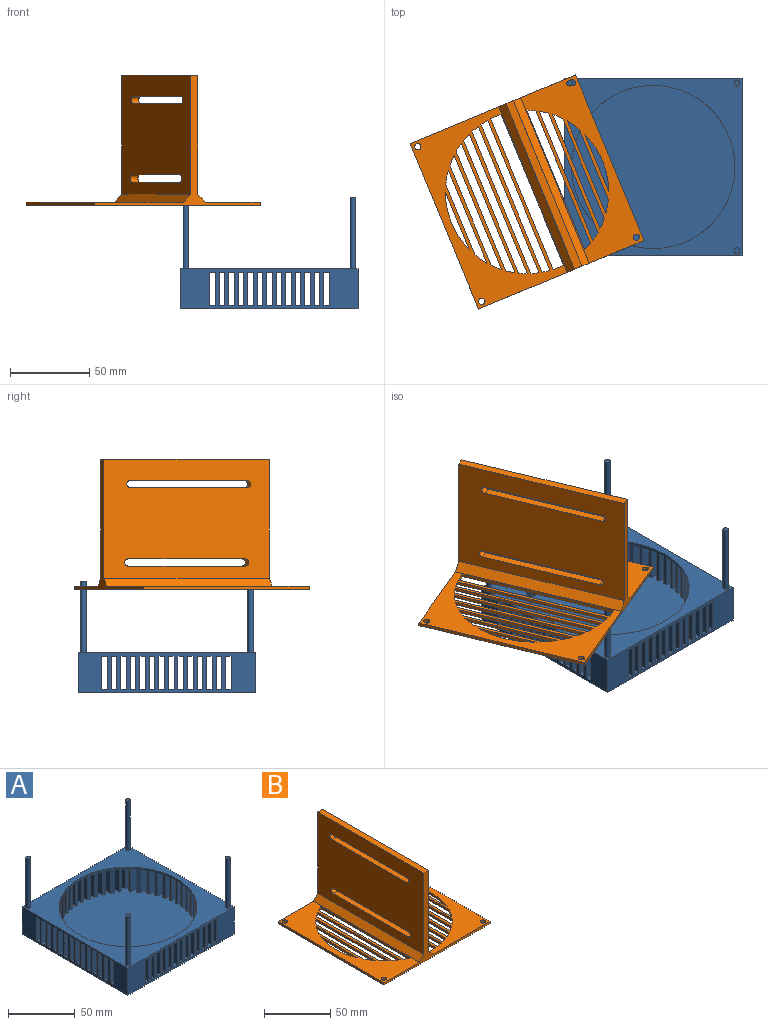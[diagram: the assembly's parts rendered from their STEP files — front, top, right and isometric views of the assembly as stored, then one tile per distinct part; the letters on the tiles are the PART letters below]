
ASSEMBLY  parts=2 mates=1
PART A: 178 faces, bbox 112x112x70 mm
  f0: plane 112x25mm, normal (0,-1,0), area 1844.5mm2, adj f9,f10,f11,f12,f22,f24,f26,f113
  f1: plane 112x25mm, normal (0,1,0), area 1844.5mm2, adj f9,f10,f11,f12,f22,f100,f102,f104
  f2: plane 21x2.5mm, normal (0,1,0), area 52.5mm2, adj f22,f24,f118,f120
  f3: plane 21x18.5mm, normal (0,-1,0), area 388.5mm2, adj f10,f22,f26,f115
  f4: plane 21x18.5mm, normal (0,1,0), area 388.5mm2, adj f10,f22,f26,f114
  f5: plane 21x2.5mm, normal (0,-1,0), area 52.5mm2, adj f22,f100,f109,f111
  f6: plane 21x2.5mm, normal (0,-1,0), area 52.5mm2, adj f22,f102,f104,f106
  f7: plane 21x18.5mm, normal (0,-1,0), area 388.5mm2, adj f10,f22,f102,f105
  f8: plane 21x18.5mm, normal (0,1,0), area 388.5mm2, adj f10,f22,f102,f103
  f9: plane 112x25mm, normal (1,0,0), area 1771mm2, adj f0,f1,f11,f12,f22,f23,f24,f25
  f10: plane 112x25mm, normal (-1,0,0), area 1771mm2, adj f0,f1,f3,f4,f7,f8,f11,f12
  f11: plane 112x112mm, normal (0,0,1), area 4173.2mm2, adj f0,f1,f9,f10,f13,f15,f17,f19
  f12: plane 112x112mm, normal (0,0,-1), area 12544mm2, adj f0,f1,f9,f10
  f13: cylinder r=1.75mm len=45mm, axis (0,0,-1), area 494.8mm2, adj f11,f14
  f14: plane 3.5x3.5mm, normal (0,0,1), area 9.6mm2, adj f13
  f15: cylinder r=1.75mm len=45mm, axis (0,0,-1), area 494.8mm2, adj f11,f16
  f16: plane 3.5x3.5mm, normal (0,0,1), area 9.6mm2, adj f15
  f17: cylinder r=1.75mm len=45mm, axis (0,0,-1), area 494.8mm2, adj f11,f18
  f18: plane 3.5x3.5mm, normal (0,0,1), area 9.6mm2, adj f17
  f19: cylinder r=1.75mm len=45mm, axis (0,0,-1), area 494.8mm2, adj f11,f20
  f20: plane 3.5x3.5mm, normal (0,0,1), area 9.6mm2, adj f19
  f21: cylinder r=51.5mm len=103mm, axis (0,0,1), area 3066.7mm2, adj f11,f22,f24,f26,f27,f28,f29,f30
  f22: plane 112x112mm, normal (0,0,1), area 10264.7mm2, adj f0,f1,f2,f3,f4,f5,f6,f7
  f23: plane 21x18mm, normal (0,1,0), area 378mm2, adj f9,f22,f24,f119
  f24: plane 27.5x21.24mm, normal (0,0,-1), area 184.2mm2, adj f0,f2,f9,f21,f23,f25,f116,f117
  f25: plane 21x18mm, normal (0,-1,0), area 378mm2, adj f9,f22,f24,f116
  f26: plane 24.19x20.7mm, normal (0,0,-1), area 133.1mm2, adj f0,f3,f4,f10,f21,f27,f113,f114
  f27: plane 21x2.19mm, normal (0,1,0), area 45.9mm2, adj f21,f22,f26,f113
  f28: plane 21x17.76mm, normal (0,1,0), area 373mm2, adj f9,f21,f22,f29
  f29: plane 17.76x3.5mm, normal (0,0,-1), area 57mm2, adj f9,f21,f28,f30
  f30: plane 21x14.88mm, normal (0,-1,0), area 312.4mm2, adj f9,f21,f22,f29
  f31: plane 17.76x3.5mm, normal (0,0,-1), area 57mm2, adj f10,f21,f32,f33
  f32: plane 21x14.88mm, normal (0,-1,0), area 312.4mm2, adj f10,f21,f22,f31
  f33: plane 21x17.76mm, normal (0,1,0), area 373mm2, adj f10,f21,f22,f31
  f34: plane 21x13.1mm, normal (0,1,0), area 275.2mm2, adj f9,f21,f22,f35
  f35: plane 13.1x3.5mm, normal (0,0,-1), area 42mm2, adj f9,f21,f34,f36
  f36: plane 21x10.98mm, normal (0,-1,0), area 230.5mm2, adj f9,f21,f22,f35
  f37: plane 13.1x3.5mm, normal (0,0,-1), area 42mm2, adj f10,f21,f38,f39
  f38: plane 21x10.98mm, normal (0,-1,0), area 230.5mm2, adj f10,f21,f22,f37
  f39: plane 21x13.1mm, normal (0,1,0), area 275.2mm2, adj f10,f21,f22,f37
  f40: plane 21x9.68mm, normal (0,1,0), area 203.2mm2, adj f9,f21,f22,f41
  f41: plane 9.68x3.5mm, normal (0,0,-1), area 31.1mm2, adj f9,f21,f40,f42
  f42: plane 21x8.13mm, normal (0,-1,0), area 170.8mm2, adj f9,f21,f22,f41
  f43: plane 9.68x3.5mm, normal (0,0,-1), area 31.1mm2, adj f10,f21,f44,f45
  f44: plane 21x8.13mm, normal (0,-1,0), area 170.8mm2, adj f10,f21,f22,f43
  f45: plane 21x9.68mm, normal (0,1,0), area 203.2mm2, adj f10,f21,f22,f43
  f46: plane 21x7.21mm, normal (0,1,0), area 151.5mm2, adj f9,f21,f22,f47
  f47: plane 7.21x3.5mm, normal (0,0,-1), area 23.3mm2, adj f9,f21,f46,f48
  f48: plane 21x6.17mm, normal (0,-1,0), area 129.5mm2, adj f9,f21,f22,f47
  f49: plane 7.21x3.5mm, normal (0,0,-1), area 23.3mm2, adj f10,f21,f50,f51
  f50: plane 21x6.17mm, normal (0,-1,0), area 129.5mm2, adj f10,f21,f22,f49
  f51: plane 21x7.21mm, normal (0,1,0), area 151.5mm2, adj f10,f21,f22,f49
  f52: plane 21x5.58mm, normal (0,1,0), area 117.2mm2, adj f9,f21,f22,f53
  f53: plane 5.58x3.5mm, normal (0,0,-1), area 18.4mm2, adj f9,f21,f52,f54
  f54: plane 21x4.98mm, normal (0,-1,0), area 104.5mm2, adj f9,f21,f22,f53
  f55: plane 5.58x3.5mm, normal (0,0,-1), area 18.4mm2, adj f10,f21,f56,f57
  f56: plane 21x4.98mm, normal (0,-1,0), area 104.5mm2, adj f10,f21,f22,f55
  f57: plane 21x5.58mm, normal (0,1,0), area 117.2mm2, adj f10,f21,f22,f55
  f58: plane 21x4.7mm, normal (0,1,0), area 98.6mm2, adj f9,f21,f22,f59
  f59: plane 4.7x3.5mm, normal (0,0,-1), area 16mm2, adj f9,f21,f58,f60
  f60: plane 21x4.51mm, normal (0,-1,0), area 94.7mm2, adj f9,f21,f22,f59
  f61: plane 4.7x3.5mm, normal (0,0,-1), area 16mm2, adj f10,f21,f62,f63
  f62: plane 21x4.51mm, normal (0,-1,0), area 94.7mm2, adj f10,f21,f22,f61
  f63: plane 21x4.7mm, normal (0,1,0), area 98.6mm2, adj f10,f21,f22,f61
  f64: plane 21x4.52mm, normal (0,1,0), area 95mm2, adj f9,f21,f22,f65
  f65: plane 4.74x3.5mm, normal (0,0,-1), area 16.1mm2, adj f9,f21,f64,f66
  f66: plane 21x4.74mm, normal (0,-1,0), area 99.6mm2, adj f9,f21,f22,f65
  f67: plane 4.74x3.5mm, normal (0,0,-1), area 16.1mm2, adj f10,f21,f68,f69
  f68: plane 21x4.74mm, normal (0,-1,0), area 99.6mm2, adj f10,f21,f22,f67
  f69: plane 21x4.52mm, normal (0,1,0), area 95mm2, adj f10,f21,f22,f67
  f70: plane 21x5.05mm, normal (0,1,0), area 106mm2, adj f9,f21,f22,f71
  f71: plane 5.69x3.5mm, normal (0,0,-1), area 18.7mm2, adj f9,f21,f70,f72
  f72: plane 21x5.69mm, normal (0,-1,0), area 119.5mm2, adj f9,f21,f22,f71
  f73: plane 5.69x3.5mm, normal (0,0,-1), area 18.7mm2, adj f10,f21,f74,f75
  f74: plane 21x5.69mm, normal (0,-1,0), area 119.5mm2, adj f10,f21,f22,f73
  f75: plane 21x5.05mm, normal (0,1,0), area 106mm2, adj f10,f21,f22,f73
  f76: plane 21x6.3mm, normal (0,1,0), area 132.3mm2, adj f9,f21,f22,f77
  f77: plane 7.39x3.5mm, normal (0,0,-1), area 23.9mm2, adj f9,f21,f76,f78
  f78: plane 21x7.39mm, normal (0,-1,0), area 155.1mm2, adj f9,f21,f22,f77
  f79: plane 7.39x3.5mm, normal (0,0,-1), area 23.9mm2, adj f10,f21,f80,f81
  f80: plane 21x7.39mm, normal (0,-1,0), area 155.1mm2, adj f10,f21,f22,f79
  f81: plane 21x6.3mm, normal (0,1,0), area 132.3mm2, adj f10,f21,f22,f79
  f82: plane 21x8.33mm, normal (0,1,0), area 175mm2, adj f9,f21,f22,f83
  f83: plane 9.92x3.5mm, normal (0,0,-1), area 31.9mm2, adj f9,f21,f82,f84
  f84: plane 21x9.92mm, normal (0,-1,0), area 208.3mm2, adj f9,f21,f22,f83
  f85: plane 9.92x3.5mm, normal (0,0,-1), area 31.9mm2, adj f10,f21,f86,f87
  f86: plane 21x9.92mm, normal (0,-1,0), area 208.3mm2, adj f10,f21,f22,f85
  f87: plane 21x8.33mm, normal (0,1,0), area 175mm2, adj f10,f21,f22,f85
  f88: plane 21x11.26mm, normal (0,1,0), area 236.4mm2, adj f9,f21,f22,f89
  f89: plane 13.44x3.5mm, normal (0,0,-1), area 43.1mm2, adj f9,f21,f88,f90
  f90: plane 21x13.44mm, normal (0,-1,0), area 282.3mm2, adj f9,f21,f22,f89
  f91: plane 13.44x3.5mm, normal (0,0,-1), area 43.1mm2, adj f10,f21,f92,f93
  f92: plane 21x13.44mm, normal (0,-1,0), area 282.3mm2, adj f10,f21,f22,f91
  f93: plane 21x11.26mm, normal (0,1,0), area 236.4mm2, adj f10,f21,f22,f91
  f94: plane 21x15.26mm, normal (0,1,0), area 320.4mm2, adj f9,f21,f22,f100
  f95: plane 21x18mm, normal (0,-1,0), area 378mm2, adj f9,f22,f100,f112
  f96: plane 18.22x3.5mm, normal (0,0,-1), area 58.4mm2, adj f10,f21,f97,f98
  f97: plane 21x18.22mm, normal (0,-1,0), area 382.6mm2, adj f10,f21,f22,f96
  f98: plane 21x15.26mm, normal (0,1,0), area 320.4mm2, adj f10,f21,f22,f96
  f99: plane 21x18mm, normal (0,1,0), area 378mm2, adj f9,f22,f100,f112
  f100: plane 27.5x24.5mm, normal (0,0,-1), area 243.9mm2, adj f1,f5,f9,f21,f94,f95,f99,f101
  f101: plane 21x18mm, normal (0,-1,0), area 378mm2, adj f9,f22,f100,f110
  f102: plane 28x20.7mm, normal (0,0,-1), area 183.2mm2, adj f1,f6,f7,f8,f10,f21,f103,f104
  f103: plane 21x2.2mm, normal (1,0,0), area 46.2mm2, adj f8,f21,f22,f102
  f104: plane 21x15mm, normal (-1,0,0), area 315mm2, adj f1,f6,f22,f102
  f105: plane 21x15mm, normal (1,0,0), area 315mm2, adj f1,f7,f22,f102
  f106: plane 21x15mm, normal (1,0,0), area 315mm2, adj f1,f6,f22,f102
  f107: plane 21x12.78mm, normal (-1,0,0), area 268.3mm2, adj f1,f21,f22,f102
  f108: plane 21x13.1mm, normal (1,0,0), area 275.2mm2, adj f1,f21,f22,f100
  f109: plane 21x15mm, normal (-1,0,0), area 315mm2, adj f1,f5,f22,f100
  f110: plane 21x15mm, normal (-1,0,0), area 315mm2, adj f1,f22,f100,f101
  f111: plane 21x15mm, normal (1,0,0), area 315mm2, adj f1,f5,f22,f100
  f112: plane 21x2.5mm, normal (-1,0,0), area 52.5mm2, adj f22,f95,f99,f100
  f113: plane 21x15.5mm, normal (-1,0,0), area 325.5mm2, adj f0,f22,f26,f27
  f114: plane 21x15.5mm, normal (1,0,0), area 325.5mm2, adj f0,f4,f22,f26
  f115: plane 21x1.7mm, normal (1,0,0), area 35.7mm2, adj f3,f21,f22,f26
  f116: plane 21x2.24mm, normal (-1,0,0), area 47mm2, adj f21,f22,f24,f25
  f117: plane 21x13.1mm, normal (1,0,0), area 275.2mm2, adj f0,f21,f22,f24
  f118: plane 21x15.5mm, normal (-1,0,0), area 325.5mm2, adj f0,f2,f22,f24
  f119: plane 21x15.5mm, normal (-1,0,0), area 325.5mm2, adj f0,f22,f23,f24
  f120: plane 21x15.5mm, normal (1,0,0), area 325.5mm2, adj f0,f2,f22,f24
  f121: plane 15.26x3.5mm, normal (0,0,-1), area 48.9mm2, adj f0,f21,f122,f123
  f122: plane 21x12.78mm, normal (-1,0,0), area 268.3mm2, adj f0,f21,f22,f121
  f123: plane 21x15.26mm, normal (1,0,0), area 320.4mm2, adj f0,f21,f22,f121
  f124: plane 21x11.26mm, normal (1,0,0), area 236.4mm2, adj f0,f21,f22,f125
  f125: plane 11.26x3.5mm, normal (0,0,-1), area 36.1mm2, adj f0,f21,f124,f126
  f126: plane 21x9.44mm, normal (-1,0,0), area 198.1mm2, adj f0,f21,f22,f125
  f127: plane 11.26x3.5mm, normal (0,0,-1), area 36.1mm2, adj f1,f21,f128,f129
  f128: plane 21x9.44mm, normal (-1,0,0), area 198.1mm2, adj f1,f21,f22,f127
  f129: plane 21x11.26mm, normal (1,0,0), area 236.4mm2, adj f1,f21,f22,f127
  f130: plane 21x8.33mm, normal (1,0,0), area 175mm2, adj f0,f21,f22,f131
  f131: plane 8.33x3.5mm, normal (0,0,-1), area 26.8mm2, adj f0,f21,f130,f132
  f132: plane 21x7.05mm, normal (-1,0,0), area 148mm2, adj f0,f21,f22,f131
  f133: plane 8.33x3.5mm, normal (0,0,-1), area 26.8mm2, adj f1,f21,f134,f135
  f134: plane 21x7.05mm, normal (-1,0,0), area 148mm2, adj f1,f21,f22,f133
  f135: plane 21x8.33mm, normal (1,0,0), area 175mm2, adj f1,f21,f22,f133
  f136: plane 21x6.3mm, normal (1,0,0), area 132.3mm2, adj f0,f21,f22,f137
  f137: plane 6.3x3.5mm, normal (0,0,-1), area 20.5mm2, adj f0,f21,f136,f138
  f138: plane 21x5.48mm, normal (-1,0,0), area 115.1mm2, adj f0,f21,f22,f137
  f139: plane 6.3x3.5mm, normal (0,0,-1), area 20.5mm2, adj f1,f21,f140,f141
  f140: plane 21x5.48mm, normal (-1,0,0), area 115.1mm2, adj f1,f21,f22,f139
  f141: plane 21x6.3mm, normal (1,0,0), area 132.3mm2, adj f1,f21,f22,f139
  f142: plane 21x5.05mm, normal (1,0,0), area 106mm2, adj f0,f21,f22,f143
  f143: plane 5.05x3.5mm, normal (0,0,-1), area 16.9mm2, adj f0,f21,f142,f144
  f144: plane 21x4.66mm, normal (-1,0,0), area 97.8mm2, adj f0,f21,f22,f143
  f145: plane 5.05x3.5mm, normal (0,0,-1), area 16.9mm2, adj f1,f21,f146,f147
  f146: plane 21x4.66mm, normal (-1,0,0), area 97.8mm2, adj f1,f21,f22,f145
  f147: plane 21x5.05mm, normal (1,0,0), area 106mm2, adj f1,f21,f22,f145
  f148: plane 21x4.52mm, normal (1,0,0), area 95mm2, adj f0,f21,f22,f149
  f149: plane 4.54x3.5mm, normal (0,0,-1), area 15.8mm2, adj f0,f21,f148,f150
  f150: plane 21x4.54mm, normal (-1,0,0), area 95.3mm2, adj f0,f21,f22,f149
  f151: plane 4.54x3.5mm, normal (0,0,-1), area 15.8mm2, adj f1,f21,f152,f153
  f152: plane 21x4.54mm, normal (-1,0,0), area 95.3mm2, adj f1,f21,f22,f151
  f153: plane 21x4.52mm, normal (1,0,0), area 95mm2, adj f1,f21,f22,f151
  f154: plane 21x4.7mm, normal (1,0,0), area 98.6mm2, adj f0,f21,f22,f155
  f155: plane 5.13x3.5mm, normal (0,0,-1), area 17.1mm2, adj f0,f21,f154,f156
  f156: plane 21x5.13mm, normal (-1,0,0), area 107.6mm2, adj f0,f21,f22,f155
  f157: plane 5.13x3.5mm, normal (0,0,-1), area 17.1mm2, adj f1,f21,f158,f159
  f158: plane 21x5.13mm, normal (-1,0,0), area 107.6mm2, adj f1,f21,f22,f157
  f159: plane 21x4.7mm, normal (1,0,0), area 98.6mm2, adj f1,f21,f22,f157
  f160: plane 21x5.58mm, normal (1,0,0), area 117.2mm2, adj f0,f21,f22,f161
  f161: plane 6.44x3.5mm, normal (0,0,-1), area 21mm2, adj f0,f21,f160,f162
  f162: plane 21x6.44mm, normal (-1,0,0), area 135.2mm2, adj f0,f21,f22,f161
  f163: plane 6.44x3.5mm, normal (0,0,-1), area 21mm2, adj f1,f21,f164,f165
  f164: plane 21x6.44mm, normal (-1,0,0), area 135.2mm2, adj f1,f21,f22,f163
  f165: plane 21x5.58mm, normal (1,0,0), area 117.2mm2, adj f1,f21,f22,f163
  f166: plane 21x7.21mm, normal (1,0,0), area 151.5mm2, adj f0,f21,f22,f167
  f167: plane 8.54x3.5mm, normal (0,0,-1), area 27.5mm2, adj f0,f21,f166,f168
  f168: plane 21x8.54mm, normal (-1,0,0), area 179.4mm2, adj f0,f21,f22,f167
  f169: plane 8.54x3.5mm, normal (0,0,-1), area 27.5mm2, adj f1,f21,f170,f171
  f170: plane 21x8.54mm, normal (-1,0,0), area 179.4mm2, adj f1,f21,f22,f169
  f171: plane 21x7.21mm, normal (1,0,0), area 151.5mm2, adj f1,f21,f22,f169
  f172: plane 21x9.68mm, normal (1,0,0), area 203.2mm2, adj f0,f21,f22,f173
  f173: plane 11.55x3.5mm, normal (0,0,-1), area 37mm2, adj f0,f21,f172,f174
  f174: plane 21x11.55mm, normal (-1,0,0), area 242.4mm2, adj f0,f21,f22,f173
  f175: plane 11.55x3.5mm, normal (0,0,-1), area 37mm2, adj f1,f21,f176,f177
  f176: plane 21x11.55mm, normal (-1,0,0), area 242.4mm2, adj f1,f21,f22,f175
  f177: plane 21x9.68mm, normal (1,0,0), area 203.2mm2, adj f1,f21,f22,f175
PART B: 72 faces, bbox 113x113x82 mm
  f0: plane 113x60.5mm, normal (0,0,1), area 3431.3mm2, adj f1,f2,f16,f17,f18,f19,f20,f21
  f1: plane 113x2mm, normal (1,0,0), area 226mm2, adj f0,f2,f56,f58
  f2: plane 113x82mm, normal (0,1,0), area 651mm2, adj f0,f1,f3,f57,f58,f59,f60,f61
  f3: plane 113x2mm, normal (-1,0,0), area 226mm2, adj f2,f56,f57,f58
  f4: plane 47.92x2mm, normal (1,0,0), area 95.8mm2, adj f5,f39,f57,f58
  f5: cylinder r=51.5mm len=7.74mm, axis (0,0,-1), area 18.5mm2, adj f4,f6,f57,f58
  f6: plane 63.4x2mm, normal (-1,0,0), area 126.8mm2, adj f5,f39,f57,f58
  f7: plane 68.21x2mm, normal (1,0,0), area 136.4mm2, adj f8,f40,f57,f58
  f8: cylinder r=51.5mm len=5mm, axis (0,0,-1), area 14.1mm2, adj f7,f9,f57,f58
  f9: plane 78.08x2mm, normal (-1,0,0), area 156.2mm2, adj f8,f40,f57,f58
  f10: plane 81.35x2mm, normal (1,0,0), area 162.7mm2, adj f11,f41,f57,f58
  f11: cylinder r=51.5mm len=5mm, axis (0,0,-1), area 12.1mm2, adj f10,f12,f57,f58
  f12: plane 88.21x2mm, normal (-1,0,0), area 176.4mm2, adj f11,f41,f57,f58
  f13: plane 90.5x2mm, normal (1,0,0), area 181mm2, adj f14,f42,f57,f58
  f14: cylinder r=51.5mm len=5mm, axis (0,0,-1), area 11.1mm2, adj f13,f15,f57,f58
  f15: plane 95.26x2mm, normal (-1,0,0), area 190.5mm2, adj f14,f42,f57,f58
  f16: plane 39.38x2mm, normal (1,0,0), area 78.8mm2, adj f0,f43,f58
  f17: plane 103.03x2mm, normal (1,0,0), area 206.1mm2, adj f0,f18,f48,f58
  f18: plane 7.18x2mm, normal (0,-1,0), area 14.4mm2, adj f0,f17,f19,f58
  f19: plane 103.03x2mm, normal (-1,0,0), area 206.1mm2, adj f0,f18,f48,f58
  f20: plane 47.92x2mm, normal (-1,0,0), area 95.8mm2, adj f0,f21,f49,f58
  f21: cylinder r=51.5mm len=7.74mm, axis (0,0,-1), area 18.5mm2, adj f0,f20,f22,f58
  f22: plane 63.4x2mm, normal (1,0,0), area 126.8mm2, adj f0,f21,f49,f58
  f23: plane 102.39x2mm, normal (1,0,0), area 204.8mm2, adj f0,f24,f50,f58
  f24: cylinder r=51.5mm len=5mm, axis (0,0,-1), area 10.1mm2, adj f0,f23,f25,f58
  f25: plane 100.8x2mm, normal (-1,0,0), area 201.6mm2, adj f0,f24,f50,f58
  f26: plane 96.81x2mm, normal (-1,0,0), area 193.6mm2, adj f0,f27,f51,f58
  f27: cylinder r=51.5mm len=5mm, axis (0,0,-1), area 10.5mm2, adj f0,f26,f28,f58
  f28: plane 99.88x2mm, normal (1,0,0), area 199.8mm2, adj f0,f27,f51,f58
  f29: plane 78.08x2mm, normal (1,0,0), area 156.2mm2, adj f0,f30,f52,f58
  f30: cylinder r=51.5mm len=5mm, axis (0,0,-1), area 14.1mm2, adj f0,f29,f31,f58
  f31: plane 68.21x2mm, normal (-1,0,0), area 136.4mm2, adj f0,f30,f52,f58
  f32: plane 90.5x2mm, normal (-1,0,0), area 181mm2, adj f0,f33,f53,f58
  f33: cylinder r=51.5mm len=5mm, axis (0,0,-1), area 11.1mm2, adj f0,f32,f34,f58
  f34: plane 95.26x2mm, normal (1,0,0), area 190.5mm2, adj f0,f33,f53,f58
  f35: plane 88.21x2mm, normal (1,0,0), area 176.4mm2, adj f0,f36,f54,f58
  f36: cylinder r=51.5mm len=5mm, axis (0,0,-1), area 12.1mm2, adj f0,f35,f37,f58
  f37: plane 81.35x2mm, normal (-1,0,0), area 162.7mm2, adj f0,f36,f54,f58
  f38: cylinder r=51.5mm len=39.38mm, axis (0,0,-1), area 80.8mm2, adj f55,f57,f58
  f39: cylinder r=51.5mm len=7.74mm, axis (0,0,-1), area 18.5mm2, adj f4,f6,f57,f58
  f40: cylinder r=51.5mm len=5mm, axis (0,0,-1), area 14.1mm2, adj f7,f9,f57,f58
  f41: cylinder r=51.5mm len=5mm, axis (0,0,-1), area 12.1mm2, adj f10,f12,f57,f58
  f42: cylinder r=51.5mm len=5mm, axis (0,0,-1), area 11.1mm2, adj f13,f15,f57,f58
  f43: cylinder r=51.5mm len=39.38mm, axis (0,0,-1), area 80.8mm2, adj f0,f16,f58
  f44: cylinder r=2mm len=4mm, axis (0,0,-1), area 25.1mm2, adj f57,f58
  f45: cylinder r=2mm len=4mm, axis (0,0,-1), area 25.1mm2, adj f0,f58
  f46: cylinder r=2mm len=4mm, axis (0,0,-1), area 25.1mm2, adj f57,f58
  f47: cylinder r=2mm len=4mm, axis (0,0,-1), area 25.1mm2, adj f0,f58
  f48: plane 7.18x2mm, normal (0,1,0), area 14.4mm2, adj f0,f17,f19,f58
  f49: cylinder r=51.5mm len=7.74mm, axis (0,0,-1), area 18.5mm2, adj f0,f20,f22,f58
  f50: cylinder r=51.5mm len=5mm, axis (0,0,-1), area 10.1mm2, adj f0,f23,f25,f58
  f51: cylinder r=51.5mm len=5mm, axis (0,0,-1), area 10.5mm2, adj f0,f26,f28,f58
  f52: cylinder r=51.5mm len=5mm, axis (0,0,-1), area 14.1mm2, adj f0,f29,f31,f58
  f53: cylinder r=51.5mm len=5mm, axis (0,0,-1), area 11.1mm2, adj f0,f32,f34,f58
  f54: cylinder r=51.5mm len=5mm, axis (0,0,-1), area 12.1mm2, adj f0,f35,f37,f58
  f55: plane 39.38x2mm, normal (-1,0,0), area 78.8mm2, adj f38,f57,f58
  f56: plane 113x82mm, normal (0,-1,0), area 651mm2, adj f0,f1,f3,f57,f58,f59,f60,f61
  f57: plane 113x37.5mm, normal (0,0,1), area 2571mm2, adj f2,f3,f4,f5,f6,f7,f8,f9
  f58: plane 113x113mm, normal (0,0,-1), area 7697.3mm2, adj f1,f2,f3,f4,f5,f6,f7,f8
  f59: plane 113x75mm, normal (1,0,0), area 7723.2mm2, adj f2,f56,f61,f62,f63,f64,f65,f66
  f60: plane 113x75mm, normal (-1,0,0), area 7723.2mm2, adj f2,f56,f61,f62,f63,f64,f65,f66
  f61: plane 113x5mm, normal (0,0,1), area 565mm2, adj f2,f56,f59,f60
  f62: plane 80x5mm, normal (0,0,1), area 400mm2, adj f59,f60,f63,f65
  f63: cylinder r=2.25mm len=5mm, axis (1,0,0), area 35.3mm2, adj f59,f60,f62,f64
  f64: plane 80x5mm, normal (0,0,-1), area 400mm2, adj f59,f60,f63,f65
  f65: cylinder r=2.25mm len=5mm, axis (1,0,0), area 35.3mm2, adj f59,f60,f62,f64
  f66: plane 80x5mm, normal (0,0,1), area 400mm2, adj f59,f60,f67,f69
  f67: cylinder r=2.25mm len=5mm, axis (1,0,0), area 35.3mm2, adj f59,f60,f66,f68
  f68: plane 80x5mm, normal (0,0,-1), area 400mm2, adj f59,f60,f67,f69
  f69: cylinder r=2.25mm len=5mm, axis (1,0,0), area 35.3mm2, adj f59,f60,f66,f68
  f70: plane 113x5mm, normal (-0.71,0,0.71), area 799mm2, adj f2,f56,f57,f60
  f71: plane 113x5mm, normal (0.71,0,0.71), area 799mm2, adj f0,f2,f56,f59
PLACE A t=(-19.72,-16.92,1.7)mm fixed
PLACE B rot(axis=(0,0,-1),157.5deg) t=(-99.29,-32.76,66.7)mm
MATE planar B.f57 <-> A.f13  axis (0,0,1) through (-53.31,-55.96,68.7)mm
